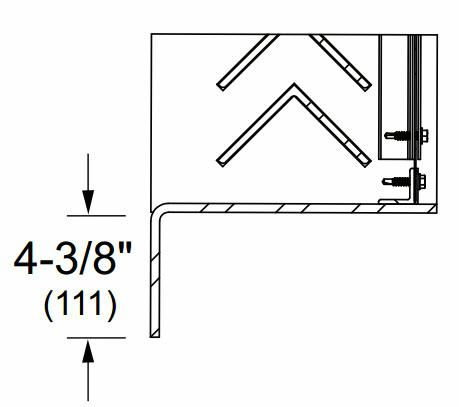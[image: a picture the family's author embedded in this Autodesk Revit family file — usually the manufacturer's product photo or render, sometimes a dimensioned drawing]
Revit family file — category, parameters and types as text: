
# Revit family: Louver_XSV-845 All-Lite
name_source: partatom
category: Mechanical Equipment
revit_build: Autodesk Revit 2013 (Build: 20120221_2030(x64)
units: mm (PartAtom-declared; Revit-internal decimal feet)

## types (1)
- XSV-845
    04 CSI = 08 91 00
    95 CSI = 10200
    Assembly Code = B2010300
    Blade Width = 2' - 11 1/2"
    Blades = Inverted V, 3/16''
    Cut Sheet = http://www.alllite.com
    Default Height = 4' - 0"
    Design Load = 290 psf
    Flange = 4-3/8''
    Frame = 8'' deep x .25'' thick
    Free Area = [48'' x 48'' unit] : 9.4 ft² 58.5%
    Height = 3' - 0"
    Height Control = 3' - 0"
    Louver = Hot Rolled A36 Steel with Zinc Rich Finish
    Louver Count = 18
    Manufacturer = Pottorff
    Max Height = 8' - 0"
    Max Width = 10' - 0"
    Maximum Size - Multiple Section = Unlimited width x single section high, Single section wide x unlimited height
    Maximum Size - Single Section = 60'' x 96'', 120'' x 60''
    Min Height = 0' - 6"
    Min Width = 0' - 6"
    Minimum Size = 6'' x 6''
    Model = XSV-845
    Mullion = Visible
    Omni Class Code = 23-60 11 17
    Omni Class Title = Exterior Louvers & Grilles
    Pressure Loss @ Beginning Point of Water Penetration = 0.06 in. wg.
    Product URL = http://www.alllite.com
    Screen = 1/2'' x .063'' expanded and flattened stainless steel
    Screen Frame = Removable
    URL = http://alllite.com
    Velocity @ .15 in. wg Pressure Loss = 755 fpm
    Warranty = http://www.alllite.com
    Width = 3' - 0"
    Width Control = 3' - 0"

## geometry (parser evidence)
native form markers: Blend x10, Sweep x2
no freeform markers — native parametric forms only
